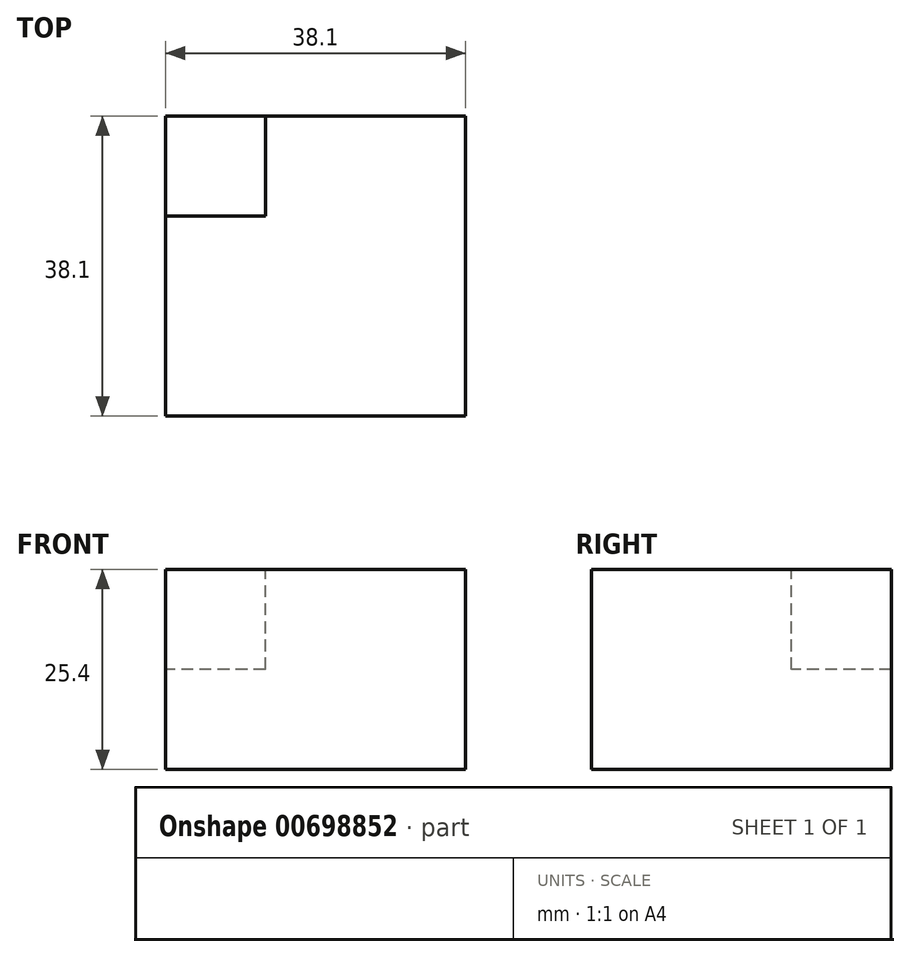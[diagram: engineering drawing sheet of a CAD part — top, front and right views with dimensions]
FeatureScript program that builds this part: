
annotation { "Feature Type Name" : "Feature", "Feature Type Description" : "" }
export const myFeature = defineFeature(function(context is Context, id is Id, definition is map)
    precondition{}
    {
        {
            var Q0;
            Q0=qCreatedBy(makeId("Top.planeOp"),FACE);
            var sketch = newSketch(context, id + "F0", { "sketchPlane" : qUnion([Q0])});
            skLineSegment(sketch, "E0", {"start": v(0, 0) * mm, "end": v(0, 38.1) * mm});
            skLineSegment(sketch, "E1", {"start": v(0, 38.1) * mm, "end": v(-38.1, 38.1) * mm});
            skLineSegment(sketch, "E2", {"start": v(-38.1, 38.1) * mm, "end": v(-38.1, 0) * mm});
            skLineSegment(sketch, "E3", {"start": v(-38.1, 0) * mm, "end": v(0, 0) * mm});
            skSolve(sketch);
        }
        {
            var Q0;
            Q0 = qSketchRegion(id + "F0", true);
            extrude(context, id + "F1", {"entities" : qUnion([Q0]), "depth" : 25.4 * mm, "offsetDistance" : 25.4 * mm});
        }
        {
            var Q0;
            Q0=makeQuery(id+"F1.opExtrude","CAP_FACE",FACE,{"disambiguationData":[OSD([sQuery(id+"F0.wireOp",EDGE,"E0"),sQuery(id+"F0.wireOp",EDGE,"E1"),sQuery(id+"F0.wireOp",EDGE,"E2"),sQuery(id+"F0.wireOp",EDGE,"E3")])],"isStart":false});
            var sketch = newSketch(context, id + "F2", { "sketchPlane" : qUnion([Q0])});
            skLineSegment(sketch, "E4.bottom", {"start": v(-38.1, 38.1) * mm, "end": v(-25.4, 38.1) * mm});
            skLineSegment(sketch, "E4.top", {"start": v(-38.1, 25.4) * mm, "end": v(-25.4, 25.4) * mm});
            skLineSegment(sketch, "E4.left", {"start": v(-38.1, 38.1) * mm, "end": v(-38.1, 25.4) * mm});
            skLineSegment(sketch, "E4.right", {"start": v(-25.4, 38.1) * mm, "end": v(-25.4, 25.4) * mm});
            skSolve(sketch);
        }
        {
            var Q0;
            Q0=makeQuery(id+"F2.imprint","IMPRINT",FACE,{"disambiguationData":[TD([[makeQuery(id+"F2.imprint","IMPRINT",EDGE,{"derivedFrom":sQuery(id+"F2.wireOp",EDGE,"E4.bottom")}),1.0]])]});
            extrude(context, id + "F3", {"entities" : qUnion([Q0]), "operationType" : NewBodyOperationType.REMOVE, "oppositeDirection" : true, "depth" : 12.7 * mm, "offsetDistance" : 25.4 * mm});
        }
    });
